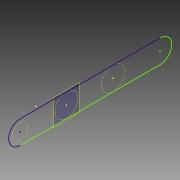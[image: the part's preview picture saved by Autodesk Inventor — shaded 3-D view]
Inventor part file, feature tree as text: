
AUTODESK INVENTOR PART (.ipt)
format: ipt  version: 2015 (Build 190159000, 159)  size: 72,192 bytes
history: native  units: in
note: dims shown in document units (in); Inventor stores cm internally (conversion verified against a paired STEP export)
features: reference x6, plane x1, sketch x1
ambient origin geometry x8: Origin, YZ Plane, XZ Plane, XY Plane, X Axis, Y Axis, Z Axis, Center Point
feature tree (8):
  plane  "Work Plane1"
  sketch  "Sketch1"
  reference  "Reference1"
  reference  "Reference2"
  reference  "Reference3"
  reference  "Reference5"
  reference  "Reference6"
  reference  "Reference7"
